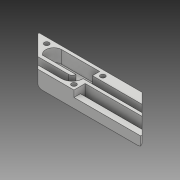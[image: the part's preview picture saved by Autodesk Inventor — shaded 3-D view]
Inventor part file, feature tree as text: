
AUTODESK INVENTOR PART (.ipt)
format: ipt  version: 2018 (Build 220112000, 112)  size: 353,792 bytes
history: native  units: mm
features: sketch x8, extrude x6, other x2, fillet x2, projected_geometry x2, shell x1, sweep x1, chamfer x1
ambient origin geometry x8: Origin, YZ Plane, XZ Plane, XY Plane, X Axis, Y Axis, Z Axis, Center Point
bodies: Body1 (feature_tree)
feature tree (23):
  other  "ソリッド1"
  extrude  "押し出し1"  TaperAngle=45.0deg  [1 undecoded]
  extrude  "押し出し3"  Depth=20.0mm
  extrude  "押し出し4"  Depth=65.0mm
  shell  "シェル1"  Thickness=20.0mm
  fillet  "フィレット2"  Radius=15.5mm
  sketch  "スケッチ7"
  extrude  "押し出し6"  Depth=3.0mm
  other  "作業平面1"
  sweep  "スイープ1"
  extrude  "押し出し7"  Depth=3.75mm
  extrude  "押し出し8"  Depth=3.75mm
  chamfer  "面取り1"  Distance=35.0mm
  fillet  "フィレット4"  Radius=10.0mm
  sketch  "スケッチ1"
  sketch  "スケッチ3"
  sketch  "スケッチ4"
  sketch  "スケッチ6"
  projected_geometry  "投影ループ1"
  sketch  "スケッチ8"
  sketch  "スケッチ9"
  sketch  "スケッチ10"
  projected_geometry  "投影ループ2"
note: 1 required parameter value undecoded (feature->parameter linkage not recoverable at this tier; creation-order binding heuristic only, values carry confidence <= 0.55)
